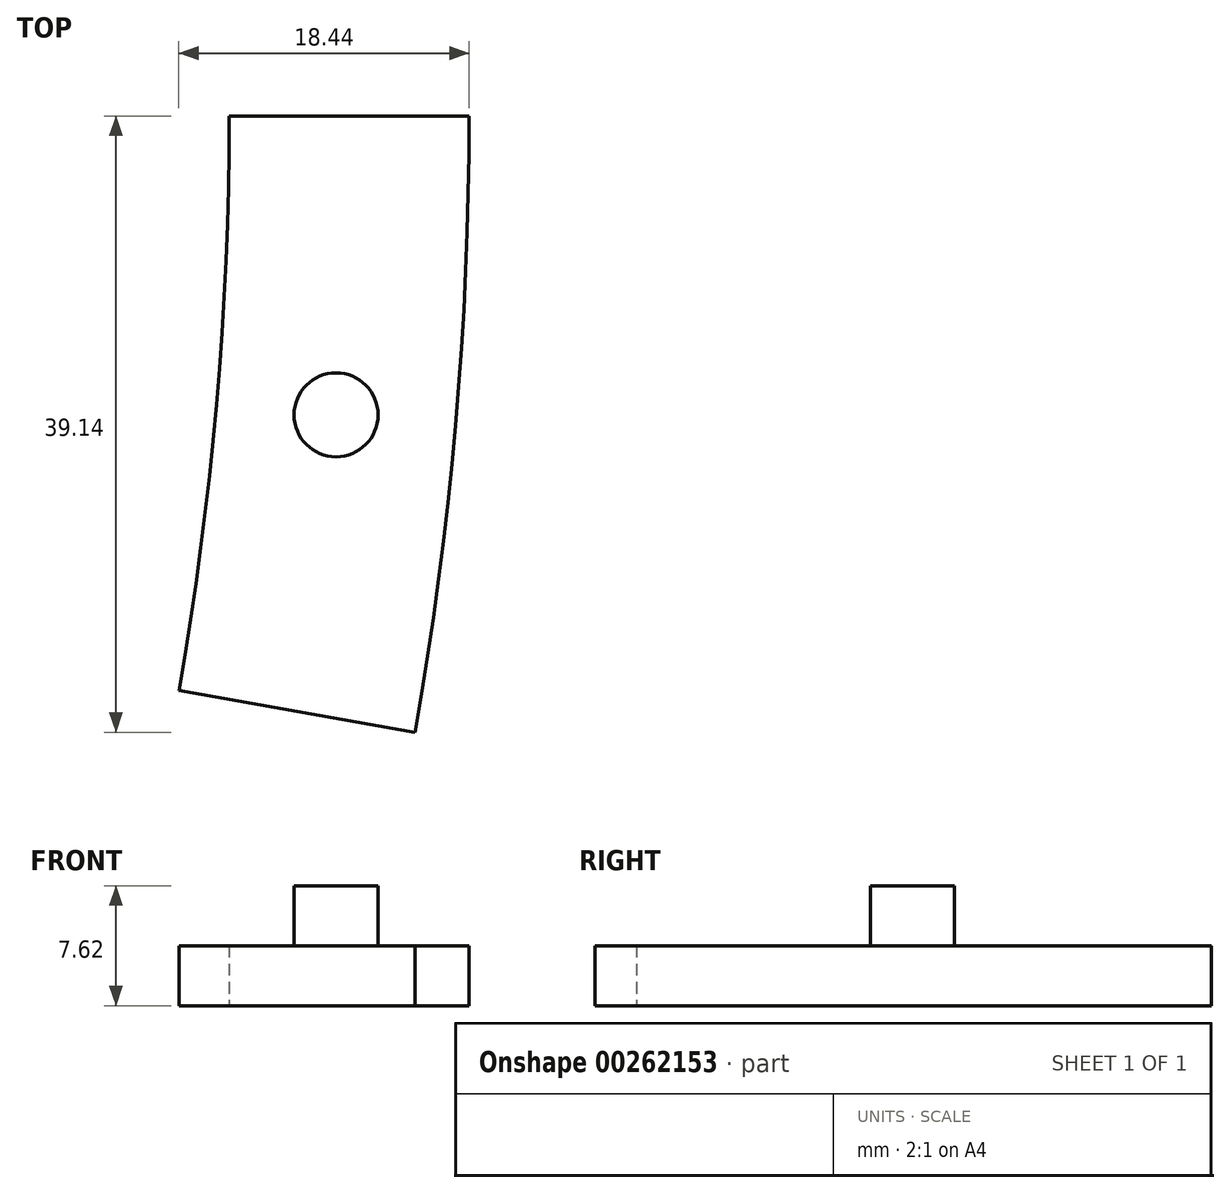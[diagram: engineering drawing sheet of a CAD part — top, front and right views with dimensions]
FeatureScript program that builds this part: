
annotation { "Feature Type Name" : "Feature", "Feature Type Description" : "" }
export const myFeature = defineFeature(function(context is Context, id is Id, definition is map)
    precondition{}
    {
        {
            var Q0;
            Q0=qCreatedBy(makeId("Top.planeOp"),FACE);
            var sketch = newSketch(context, id + "F0", { "sketchPlane" : qUnion([Q0])});
            skCircle(sketch, "E0", {"center": v(0, 0) * mm, "radius": 225.42 * mm});
            skCircle(sketch, "E1", {"center": v(0, 0) * mm, "radius": 210.19 * mm});
            skCircle(sketch, "E2", {"center": v(0, 0) * mm, "radius": 217.8 * mm, "construction": true});
            skLineSegment(sketch, "E3", {"start": v(0, 0) * mm, "end": v(225.42, 0) * mm});
            skLineSegment(sketch, "E4", {"start": v(0, 0) * mm, "end": v(222, -39.14) * mm});
            skLineSegment(sketch, "E5", {"start": v(0, 0) * mm, "end": v(224.57, -19.65) * mm, "construction": true});
            skCircle(sketch, "E6", {"center": v(216.98, -18.98) * mm, "radius": 2.67 * mm});
            skSolve(sketch);
        }
        {
            var Q0;
            Q0=makeQuery(id+"F0.imprint","IMPRINT",FACE,{"disambiguationData":[TD([[makeQuery(id+"F0.imprint","IMPRINT",EDGE,{"derivedFrom":sQuery(id+"F0.wireOp",EDGE,"E6")}),-1.0]])]});
            extrude(context, id + "F1", {"entities" : qUnion([Q0]), "depth" : 3.8 * mm});
        }
        {
            var Q0;
            Q0=makeQuery(id+"F0.imprint","IMPRINT",FACE,{"disambiguationData":[TD([[makeQuery(id+"F0.imprint","IMPRINT",EDGE,{"derivedFrom":sQuery(id+"F0.wireOp",EDGE,"E6")}),1.0]])]});
            extrude(context, id + "F2", {"entities" : qUnion([Q0]), "operationType" : NewBodyOperationType.ADD, "depth" : 7.62 * mm});
        }
    });
